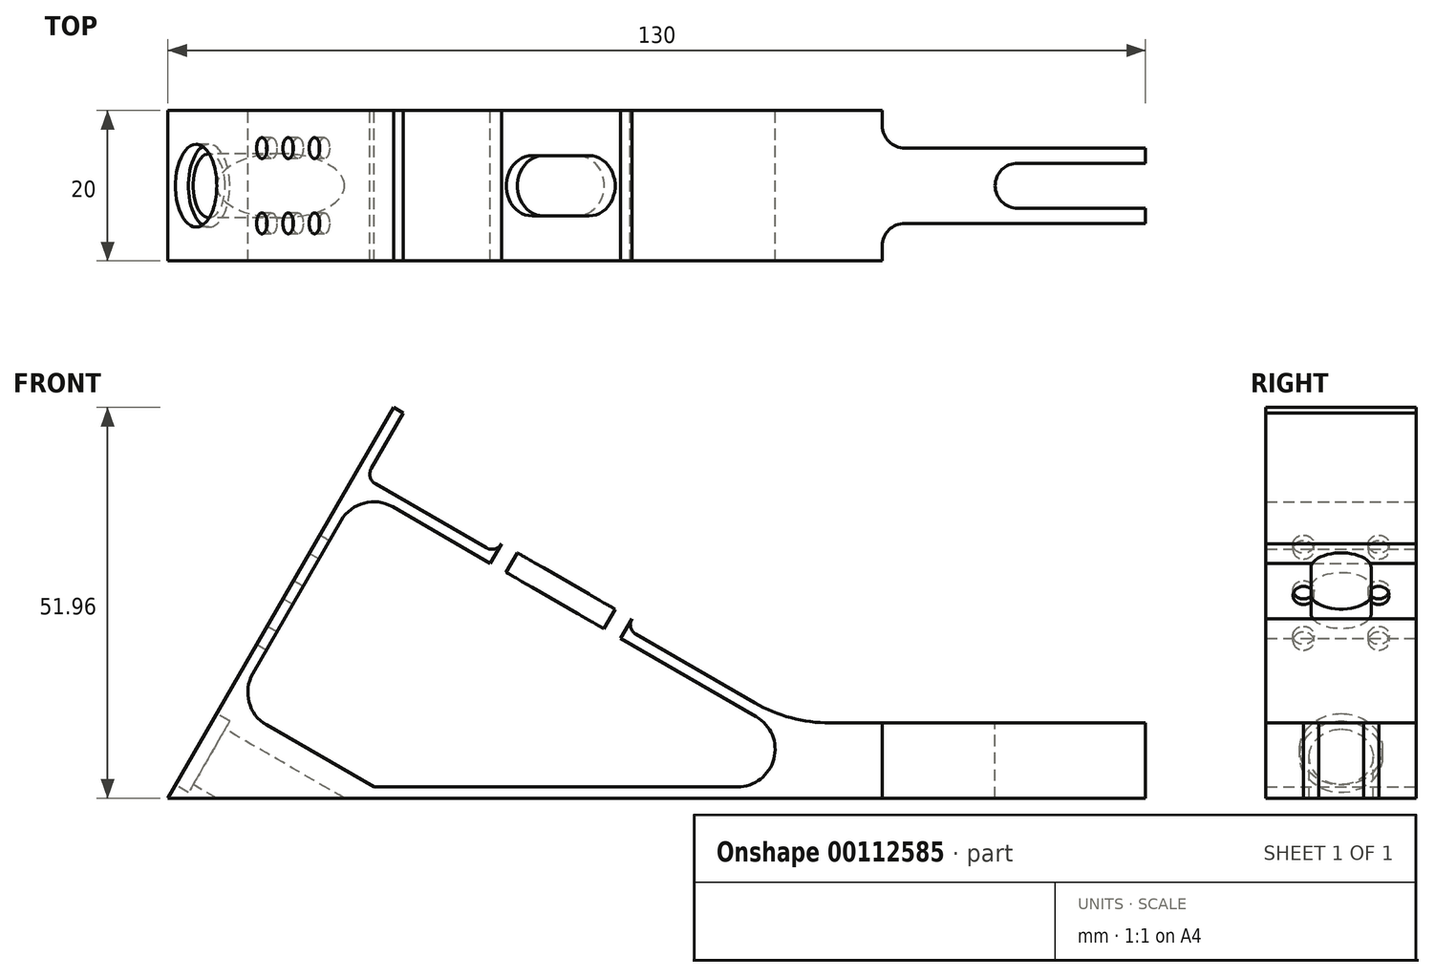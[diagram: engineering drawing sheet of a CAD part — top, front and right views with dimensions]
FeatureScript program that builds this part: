
annotation { "Feature Type Name" : "Feature", "Feature Type Description" : "" }
export const myFeature = defineFeature(function(context is Context, id is Id, definition is map)
    precondition{}
    {
        {
            var Q0;
            Q0=qCreatedBy(makeId("Front.planeOp"),FACE);
            var sketch = newSketch(context, id + "F0", { "sketchPlane" : qUnion([Q0])});
            skLineSegment(sketch, "E0", {"start": v(0, 0) * mm, "end": v(30, 51.96) * mm});
            skLineSegment(sketch, "E1", {"start": v(30, 51.96) * mm, "end": v(31.3, 51.21) * mm});
            skLineSegment(sketch, "E2", {"start": v(31.3, 51.21) * mm, "end": v(27.05, 43.85) * mm});
            skLineSegment(sketch, "E3", {"start": v(27.6, 41.8) * mm, "end": v(42.32, 33.3) * mm});
            skLineSegment(sketch, "E4", {"start": v(44.37, 33.85) * mm, "end": v(61.7, 23.85) * mm});
            skLineSegment(sketch, "E5", {"start": v(61.7, 23.85) * mm, "end": v(61.7, 23.85) * mm});
            skLineSegment(sketch, "E6", {"start": v(62.24, 21.8) * mm, "end": v(78.04, 12.68) * mm});
            skLineSegment(sketch, "E7", {"start": v(88.04, 10) * mm, "end": v(130, 10) * mm});
            skLineSegment(sketch, "E8", {"start": v(130, 10) * mm, "end": v(130, 0) * mm});
            skLineSegment(sketch, "E9", {"start": v(0, 0) * mm, "end": v(130, 0) * mm});
            skLineSegment(sketch, "E10", {"start": v(23.05, 36.92) * mm, "end": v(11.3, 16.57) * mm});
            skLineSegment(sketch, "E11", {"start": v(13.13, 9.74) * mm, "end": v(27.4, 1.5) * mm});
            skLineSegment(sketch, "E12", {"start": v(27.4, 1.5) * mm, "end": v(75.74, 1.5) * mm});
            skLineSegment(sketch, "E13", {"start": v(78.24, 10.83) * mm, "end": v(29.88, 38.75) * mm});
            skPoint(sketch, "E14.visualSharp", {"position": v(94.4, 1.5) * mm});
            skArc(sketch, "E14.filletArc", {"start": v(75.74, 1.5) * mm, "mid": v(80.57, 5.2) * mm, "end": v(78.24, 10.83) * mm});
            skPoint(sketch, "E15.visualSharp", {"position": v(25.55, 41.25) * mm});
            skArc(sketch, "E15.filletArc", {"start": v(29.88, 38.75) * mm, "mid": v(26.09, 39.25) * mm, "end": v(23.05, 36.92) * mm});
            skPoint(sketch, "E16.visualSharp", {"position": v(8.8, 12.24) * mm});
            skArc(sketch, "E16.filletArc", {"start": v(11.3, 16.57) * mm, "mid": v(10.8, 12.78) * mm, "end": v(13.13, 9.74) * mm});
            skLineSegment(sketch, "E17", {"start": v(44.37, 33.85) * mm, "end": v(44.37, 33.85) * mm});
            skPoint(sketch, "E18.visualSharp", {"position": v(26.3, 42.55) * mm});
            skArc(sketch, "E18.filletArc", {"start": v(27.05, 43.85) * mm, "mid": v(26.9, 42.71) * mm, "end": v(27.6, 41.8) * mm});
            skPoint(sketch, "E19.visualSharp", {"position": v(43.62, 32.55) * mm});
            skArc(sketch, "E19.filletArc", {"start": v(42.32, 33.3) * mm, "mid": v(43.46, 33.15) * mm, "end": v(44.37, 33.85) * mm});
            skPoint(sketch, "E20.visualSharp", {"position": v(60.94, 22.55) * mm});
            skArc(sketch, "E20.filletArc", {"start": v(61.7, 23.85) * mm, "mid": v(61.54, 22.71) * mm, "end": v(62.24, 21.8) * mm});
            skPoint(sketch, "E21.visualSharp", {"position": v(82.68, 10) * mm});
            skArc(sketch, "E21.filletArc", {"start": v(78.04, 12.68) * mm, "mid": v(82.86, 10.68) * mm, "end": v(88.04, 10) * mm});
            skSolve(sketch);
        }
        {
            var Q0;
            Q0=makeQuery(id+"F0.imprint","IMPRINT",FACE,{"disambiguationData":[TD([[makeQuery(id+"F0.imprint","IMPRINT",EDGE,{"derivedFrom":sQuery(id+"F0.wireOp",EDGE,"E0")}),-1.0]])]});
            extrude(context, id + "F1", {"entities" : qUnion([Q0]), "depth" : 20 * mm, "symmetric" : true});
        }
        {
            var Q0;
            Q0=makeQuery(id+"F1.opExtrude","SWEPT_FACE",FACE,{"disambiguationData":[OSD([sQuery(id+"F0.wireOp",EDGE,"E7")])]});
            var sketch = newSketch(context, id + "F2", { "sketchPlane" : qUnion([Q0])});
            skLineSegment(sketch, "E22", {"start": v(130, 5) * mm, "end": v(98, 5) * mm});
            skLineSegment(sketch, "E23", {"start": v(95, 8) * mm, "end": v(95, 10) * mm});
            skLineSegment(sketch, "E24", {"start": v(95, -10) * mm, "end": v(95, -8) * mm});
            skLineSegment(sketch, "E25", {"start": v(98, -5) * mm, "end": v(130, -5) * mm});
            skLineSegment(sketch, "E26", {"start": v(130, -3) * mm, "end": v(113, -3) * mm});
            skLineSegment(sketch, "E27", {"start": v(130, 3) * mm, "end": v(113, 3) * mm});
            skArc(sketch, "E28", {"start": v(113, 3) * mm, "mid": v(110, 0) * mm, "end": v(113, -3) * mm});
            skPoint(sketch, "E29.visualSharp", {"position": v(95, -5) * mm});
            skArc(sketch, "E29.filletArc", {"start": v(98, -5) * mm, "mid": v(95.88, -5.88) * mm, "end": v(95, -8) * mm});
            skPoint(sketch, "E30.visualSharp", {"position": v(95, 5) * mm});
            skArc(sketch, "E30.filletArc", {"start": v(95, 8) * mm, "mid": v(95.88, 5.88) * mm, "end": v(98, 5) * mm});
            skLineSegment(sketch, "E31", {"start": v(130, -5) * mm, "end": v(130, -3) * mm});
            skLineSegment(sketch, "E32", {"start": v(130, 3) * mm, "end": v(130, 5) * mm});
            skSolve(sketch);
        }
        {
            var Q0;
            {var subQ5=sQuery(id+"F2.wireOp",EDGE,"E24");Q0=makeQuery(id+"F2.imprint","IMPRINT",FACE,{"disambiguationData":[TD([[makeQuery(id+"F2.imprint","IMPRINT",EDGE,{"derivedFrom":subQ5}),-1.0]])]});}
            var Q1;
            {var subQ0=sQuery(id+"F2.wireOp",EDGE,"E26");Q1=makeQuery(id+"F2.imprint","IMPRINT",FACE,{"disambiguationData":[TD([[makeQuery(id+"F2.imprint","IMPRINT",EDGE,{"derivedFrom":subQ0}),-1.0]])]});}
            var Q2;
            {var subQ4=sQuery(id+"F2.wireOp",EDGE,"E22");Q2=makeQuery(id+"F2.imprint","IMPRINT",FACE,{"disambiguationData":[TD([[makeQuery(id+"F2.imprint","IMPRINT",EDGE,{"derivedFrom":subQ4}),-1.0]])]});}
            extrude(context, id + "F3", {"entities" : qUnion([Q0, Q1, Q2]), "operationType" : NewBodyOperationType.REMOVE, "endBound" : BoundingType.THROUGH_ALL, "oppositeDirection" : true, "depth" : 25 * mm});
        }
        {
            var Q0;
            Q0=makeQuery(id+"F1.opExtrude","SWEPT_FACE",FACE,{"disambiguationData":[OSD([sQuery(id+"F0.wireOp",EDGE,"E0")])]});
            var sketch = newSketch(context, id + "F4", { "sketchPlane" : qUnion([Q0])});
            skCircle(sketch, "E33", {"center": v(0, 7.5) * mm, "radius": 5.5 * mm});
            skCircle(sketch, "E34", {"center": v(0, 7.5) * mm, "radius": 4.25 * mm});
            skLineSegment(sketch, "E35", {"start": v(0, 56.88) * mm, "end": v(0, -11.19) * mm, "construction": true});
            skSolve(sketch);
        }
        {
            var Q0;
            Q0=makeQuery(id+"F4.imprint","IMPRINT",FACE,{"disambiguationData":[TD([[makeQuery(id+"F4.imprint","IMPRINT",EDGE,{"derivedFrom":sQuery(id+"F4.wireOp",EDGE,"E33")}),1.0]])]});
            extrude(context, id + "F5", {"entities" : qUnion([Q0]), "operationType" : NewBodyOperationType.REMOVE, "oppositeDirection" : true, "depth" : 2 * mm});
        }
        {
            var Q0;
            Q0=makeQuery(id+"F5.boolean.opBoolean","SPLIT",FACE,{"disambiguationData":[TD([makeQuery(id+"F5.opExtrude","SWEPT_FACE",FACE,{"disambiguationData":[OSD([sQuery(id+"F4.wireOp",EDGE,"E34")])]})])],"derivedFrom":makeQuery(id+"F1.opExtrude","SWEPT_FACE",FACE,{"disambiguationData":[OSD([sQuery(id+"F0.wireOp",EDGE,"E0")])]})});
            extrude(context, id + "F6", {"entities" : qUnion([Q0]), "operationType" : NewBodyOperationType.REMOVE, "endBound" : BoundingType.THROUGH_ALL, "oppositeDirection" : true, "depth" : 25 * mm});
        }
        {
            var Q0;
            {var subQ1=sQuery(id+"F0.wireOp",EDGE,"E1");var subQ19=sQuery(id+"F0.wireOp",EDGE,"E0");Q0=makeQuery(id+"F5.boolean.opBoolean","SPLIT",FACE,{"disambiguationData":[TD([makeQuery(id+"F1.opExtrude","SWEPT_FACE",FACE,{"disambiguationData":[OSD([subQ1])]})])],"derivedFrom":makeQuery(id+"F1.opExtrude","SWEPT_FACE",FACE,{"disambiguationData":[OSD([subQ19])]})});}
            var sketch = newSketch(context, id + "F7", { "sketchPlane" : qUnion([Q0])});
            skLineSegment(sketch, "E36", {"start": v(-5, 60) * mm, "end": v(-5, 15.55) * mm, "construction": true});
            skLineSegment(sketch, "E37", {"start": v(5, 59.05) * mm, "end": v(5, 14.76) * mm, "construction": true});
            skLineSegment(sketch, "E38", {"start": v(0, 62.32) * mm, "end": v(0, 9.9) * mm, "construction": true});
            skCircle(sketch, "E39", {"center": v(-5, 25) * mm, "radius": 1.4 * mm});
            skCircle(sketch, "E40", {"center": v(-5, 32) * mm, "radius": 1.4 * mm});
            skCircle(sketch, "E41", {"center": v(-5, 39) * mm, "radius": 1.4 * mm});
            skCircle(sketch, "E42", {"center": v(5, 39) * mm, "radius": 1.4 * mm});
            skCircle(sketch, "E43", {"center": v(5, 32) * mm, "radius": 1.4 * mm});
            skCircle(sketch, "E44", {"center": v(5, 25) * mm, "radius": 1.4 * mm});
            skSolve(sketch);
        }
        {
            var Q0;
            Q0=makeQuery(id+"F7.imprint","IMPRINT",FACE,{"disambiguationData":[TD([[makeQuery(id+"F7.imprint","IMPRINT",EDGE,{"derivedFrom":sQuery(id+"F7.wireOp",EDGE,"E40")}),1.0]])]});
            var Q1;
            Q1=makeQuery(id+"F7.imprint","IMPRINT",FACE,{"disambiguationData":[TD([[makeQuery(id+"F7.imprint","IMPRINT",EDGE,{"derivedFrom":sQuery(id+"F7.wireOp",EDGE,"E39")}),1.0]])]});
            var Q2;
            Q2=makeQuery(id+"F7.imprint","IMPRINT",FACE,{"disambiguationData":[TD([[makeQuery(id+"F7.imprint","IMPRINT",EDGE,{"derivedFrom":sQuery(id+"F7.wireOp",EDGE,"E41")}),1.0]])]});
            extrude(context, id + "F8", {"entities" : qUnion([Q0, Q1, Q2]), "operationType" : NewBodyOperationType.REMOVE, "endBound" : BoundingType.UP_TO_NEXT, "oppositeDirection" : true, "depth" : 25 * mm});
        }
        {
            var Q0;
            Q0 = qSketchRegion(id + "F7", true);
            extrude(context, id + "F9", {"entities" : qUnion([Q0]), "operationType" : NewBodyOperationType.REMOVE, "oppositeDirection" : true, "depth" : 25 * mm});
        }
        {
            var Q0;
            Q0=makeQuery(id+"F1.opExtrude","SWEPT_FACE",FACE,{"disambiguationData":[OSD([sQuery(id+"F0.wireOp",EDGE,"E4")])]});
            var sketch = newSketch(context, id + "F10", { "sketchPlane" : qUnion([Q0])});
            skLineSegment(sketch, "E45", {"start": v(27.93, 0) * mm, "end": v(34.93, 0) * mm, "construction": true});
            skLineSegment(sketch, "E46.0", {"start": v(21.5, -10) * mm, "end": v(41.5, -10) * mm});
            skLineSegment(sketch, "E47.0", {"start": v(3, -10) * mm, "end": v(20, -10) * mm});
            skLineSegment(sketch, "E48.0", {"start": v(0, -10) * mm, "end": v(0, 10) * mm});
            skLineSegment(sketch, "E49.0", {"start": v(3, 10) * mm, "end": v(20, 10) * mm});
            skLineSegment(sketch, "E50.0", {"start": v(21.5, 10) * mm, "end": v(41.5, 10) * mm});
            skArc(sketch, "E51.0.startCap", {"start": v(27.93, -4) * mm, "mid": v(23.93, 0) * mm, "end": v(27.93, 4) * mm});
            skArc(sketch, "E51.0.endCap", {"start": v(34.93, 4) * mm, "mid": v(38.93, 0) * mm, "end": v(34.93, -4) * mm});
            skLineSegment(sketch, "E51.0.left", {"start": v(27.93, 4) * mm, "end": v(34.93, 4) * mm});
            skLineSegment(sketch, "E51.0.right", {"start": v(27.93, -4) * mm, "end": v(34.93, -4) * mm});
            skSolve(sketch);
        }
        {
            var Q0;
            Q0=makeQuery(id+"F10.imprint","IMPRINT",FACE,{"disambiguationData":[TD([[makeQuery(id+"F10.imprint","IMPRINT",EDGE,{"derivedFrom":sQuery(id+"F10.wireOp",EDGE,"E51.0.startCap")}),-1.0]])]});
            extrude(context, id + "F11", {"entities" : qUnion([Q0]), "operationType" : NewBodyOperationType.REMOVE, "endBound" : BoundingType.UP_TO_NEXT, "oppositeDirection" : true, "depth" : 25 * mm});
        }
    });
